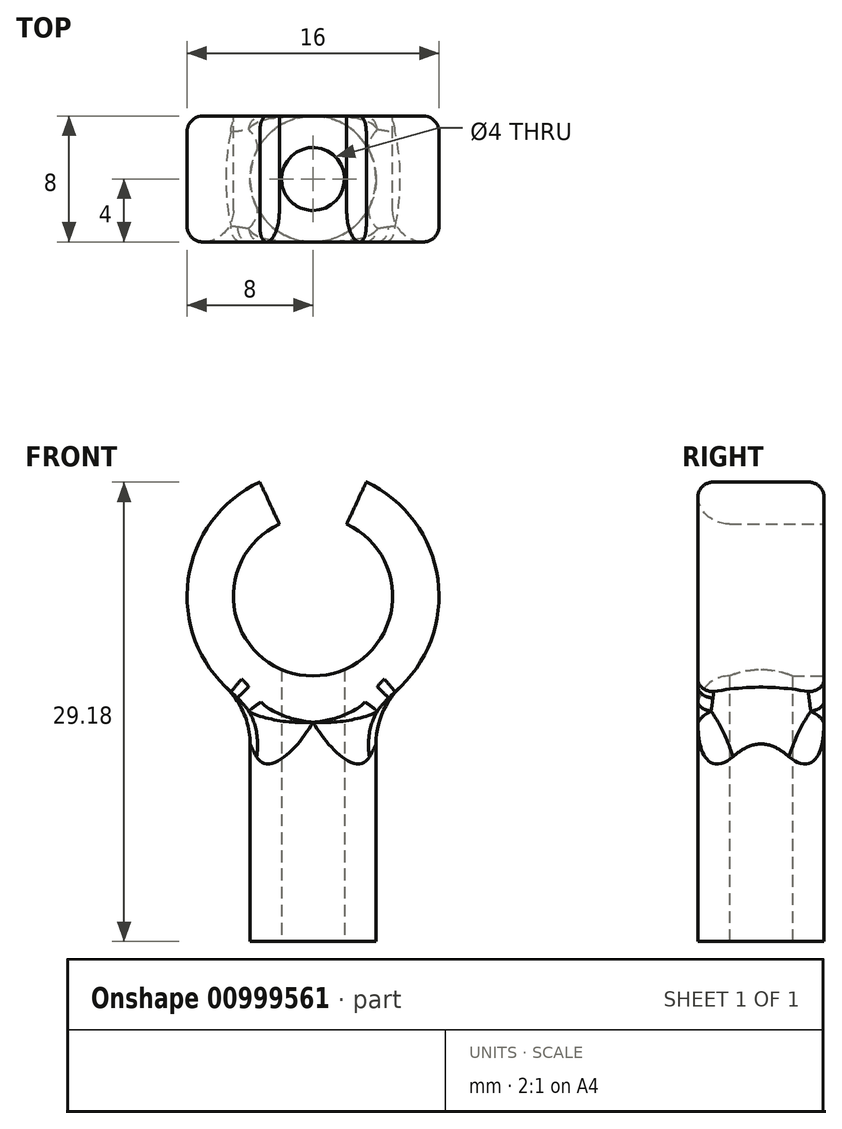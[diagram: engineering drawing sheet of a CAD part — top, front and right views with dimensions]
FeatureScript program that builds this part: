
annotation { "Feature Type Name" : "Feature", "Feature Type Description" : "" }
export const myFeature = defineFeature(function(context is Context, id is Id, definition is map)
    precondition{}
    {
        {
            var Q0;
            Q0=qCreatedBy(makeId("Top.planeOp"),FACE);
            var sketch = newSketch(context, id + "F0", { "sketchPlane" : qUnion([Q0])});
            skCircle(sketch, "E0", {"center": v(0, 0) * mm, "radius": 4 * mm});
            skSolve(sketch);
        }
        {
            var Q0;
            Q0=makeQuery(id+"F0.imprint","IMPRINT",FACE,{"disambiguationData":[TD([[makeQuery(id+"F0.imprint","IMPRINT",EDGE,{"derivedFrom":sQuery(id+"F0.wireOp",EDGE,"E0")}),1.0]])]});
            extrude(context, id + "F1", {"entities" : qUnion([Q0]), "oppositeDirection" : true, "depth" : 15 * mm, "offsetDistance" : 25 * mm});
        }
        {
            var Q0;
            Q0=qCreatedBy(makeId("Front.planeOp"),FACE);
            var sketch = newSketch(context, id + "F2", { "sketchPlane" : qUnion([Q0])});
            skPoint(sketch, "E1", {"position": v(-4, 0) * mm});
            skPoint(sketch, "E2", {"position": v(0, 0) * mm});
            skPoint(sketch, "E3", {"position": v(0, 6.93) * mm});
            skCircle(sketch, "E4", {"center": v(0, 6.93) * mm, "radius": 8 * mm});
            skSolve(sketch);
        }
        {
            var Q0;
            Q0=makeQuery(id+"F2.imprint","IMPRINT",FACE,{"disambiguationData":[TD([[makeQuery(id+"F2.imprint","IMPRINT",EDGE,{"derivedFrom":sQuery(id+"F2.wireOp",EDGE,"E4")}),1.0]])]});
            extrude(context, id + "F3", {"entities" : qUnion([Q0]), "operationType" : NewBodyOperationType.ADD, "endBound" : BoundingType.SYMMETRIC, "depth" : 8 * mm, "offsetDistance" : 25 * mm});
        }
        {
            var Q0;
            Q0=makeQuery(id+"F3.opExtrude","CAP_FACE",FACE,{"disambiguationData":[OSD([sQuery(id+"F2.wireOp",EDGE,"E4")])],"isStart":true});
            var sketch = newSketch(context, id + "F4", { "sketchPlane" : qUnion([Q0])});
            skPoint(sketch, "E5", {"position": v(0, 6.93) * mm});
            skArc(sketch, "E6", {"start": v(-2.14, 11.51) * mm, "mid": v(0, 1.87) * mm, "end": v(2.14, 11.51) * mm});
            skLineSegment(sketch, "E7", {"start": v(-2.14, 11.51) * mm, "end": v(-3.38, 14.18) * mm});
            skLineSegment(sketch, "E8", {"start": v(0, 0) * mm, "end": v(0, 28.53) * mm, "construction": true});
            skLineSegment(sketch, "E9.MirrorCS", {"start": v(2.14, 11.51) * mm, "end": v(3.38, 14.18) * mm});
            skArc(sketch, "E10", {"start": v(3.38, 14.18) * mm, "mid": v(0, 15.13) * mm, "end": v(-3.38, 14.18) * mm});
            skPoint(sketch, "E11.orphan", {"position": v(-8.62, 25.42) * mm});
            skPoint(sketch, "E12.orphan", {"position": v(8.62, 25.42) * mm});
            skSolve(sketch);
        }
        {
            var Q0;
            Q0=makeQuery(id+"F4.imprint","IMPRINT",FACE,{"disambiguationData":[TD([[makeQuery(id+"F4.imprint","IMPRINT",EDGE,{"derivedFrom":sQuery(id+"F4.wireOp",EDGE,"E6")}),1.0]])]});
            extrude(context, id + "F5", {"entities" : qUnion([Q0]), "operationType" : NewBodyOperationType.REMOVE, "oppositeDirection" : true, "depth" : 25 * mm, "offsetDistance" : 25 * mm});
        }
        {
            var Q0;
            Q0=makeQuery(id+"F1.opExtrude","CAP_FACE",FACE,{"disambiguationData":[OSD([sQuery(id+"F0.wireOp",EDGE,"E0")])],"isStart":false});
            var sketch = newSketch(context, id + "F6", { "sketchPlane" : qUnion([Q0])});
            skCircle(sketch, "E13", {"center": v(0, 0) * mm, "radius": 2 * mm});
            skSolve(sketch);
        }
        {
            var Q0;
            Q0 = qSketchRegion(id + "F6", true);
            extrude(context, id + "F7", {"entities" : qUnion([Q0]), "operationType" : NewBodyOperationType.REMOVE, "oppositeDirection" : true, "depth" : 20 * mm, "offsetDistance" : 25 * mm});
        }
        {
            var Q0;
            Q0=makeQuery(id+"F3.boolean.opBoolean","INTERSECT",EDGE,{"disambiguationData":[OD(1.0)],"derivedFrom":[makeQuery(id+"F1.opExtrude","SWEPT_FACE",FACE,{"disambiguationData":[OSD([sQuery(id+"F0.wireOp",EDGE,"E0")])]}),makeQuery(id+"F3.opExtrude","SWEPT_FACE",FACE,{"disambiguationData":[OSD([sQuery(id+"F2.wireOp",EDGE,"E4")])]})]});
            fillet(context, id + "F8", {"entities" : qUnion([Q0]), "radius" : 5 * mm, "tangentPropagation" : true, "allowEdgeOverflow" : false});
        }
        {
            var Q0;
            Q0=makeQuery(id+"F5.boolean.opBoolean","INTERSECT",EDGE,{"derivedFrom":[makeQuery(id+"F3.opExtrude","CAP_FACE",FACE,{"disambiguationData":[OSD([sQuery(id+"F2.wireOp",EDGE,"E4")])],"isStart":false}),makeQuery(id+"F5.opExtrude","SWEPT_FACE",FACE,{"disambiguationData":[OSD([sQuery(id+"F4.wireOp",EDGE,"E6")])]})]});
            var Q1;
            Q1=makeQuery(id+"F5.boolean.opBoolean","COPY",EDGE,{"derivedFrom":makeQuery(id+"F5.opExtrude","CAP_EDGE",EDGE,{"disambiguationData":[OSD([sQuery(id+"F4.wireOp",EDGE,"E6")])],"isStart":true})});
            fillet(context, id + "F9", {"entities" : qUnion([Q0, Q1]), "radius" : 2 * mm, "tangentPropagation" : true, "allowEdgeOverflow" : false});
        }
        {
            var Q0;
            {var subQ0=sQuery(id+"F2.wireOp",EDGE,"E4");Q0=makeQuery(id+"F5.boolean.opBoolean","SPLIT",EDGE,{"disambiguationData":[TD([makeQuery(id+"F5.opExtrude","SWEPT_FACE",FACE,{"disambiguationData":[OSD([sQuery(id+"F4.wireOp",EDGE,"E9.MirrorCS")])]})])],"derivedFrom":makeQuery(id+"F3.opExtrude","CAP_EDGE",EDGE,{"disambiguationData":[OSD([subQ0])],"isStart":false})});}
            var Q1;
            {var subQ0=sQuery(id+"F2.wireOp",EDGE,"E4");Q1=makeQuery(id+"F5.boolean.opBoolean","SPLIT",EDGE,{"disambiguationData":[TD([makeQuery(id+"F5.opExtrude","SWEPT_FACE",FACE,{"disambiguationData":[OSD([sQuery(id+"F4.wireOp",EDGE,"E7")])]})])],"derivedFrom":makeQuery(id+"F3.opExtrude","CAP_EDGE",EDGE,{"disambiguationData":[OSD([subQ0])],"isStart":false})});}
            var Q2;
            {var subQ0=sQuery(id+"F2.wireOp",EDGE,"E4");Q2=makeQuery(id+"F5.boolean.opBoolean","SPLIT",EDGE,{"disambiguationData":[TD([makeQuery(id+"F5.opExtrude","SWEPT_FACE",FACE,{"disambiguationData":[OSD([sQuery(id+"F4.wireOp",EDGE,"E9.MirrorCS")])]})])],"derivedFrom":makeQuery(id+"F3.opExtrude","CAP_EDGE",EDGE,{"disambiguationData":[OSD([subQ0])],"isStart":true})});}
            var Q3;
            {var subQ0=sQuery(id+"F2.wireOp",EDGE,"E4");Q3=makeQuery(id+"F5.boolean.opBoolean","SPLIT",EDGE,{"disambiguationData":[TD([makeQuery(id+"F5.opExtrude","SWEPT_FACE",FACE,{"disambiguationData":[OSD([sQuery(id+"F4.wireOp",EDGE,"E7")])]})])],"derivedFrom":makeQuery(id+"F3.opExtrude","CAP_EDGE",EDGE,{"disambiguationData":[OSD([subQ0])],"isStart":true})});}
            fillet(context, id + "F10", {"entities" : qUnion([Q0, Q1, Q2, Q3]), "radius" : 1 * mm, "tangentPropagation" : true, "allowEdgeOverflow" : false});
        }
    });
